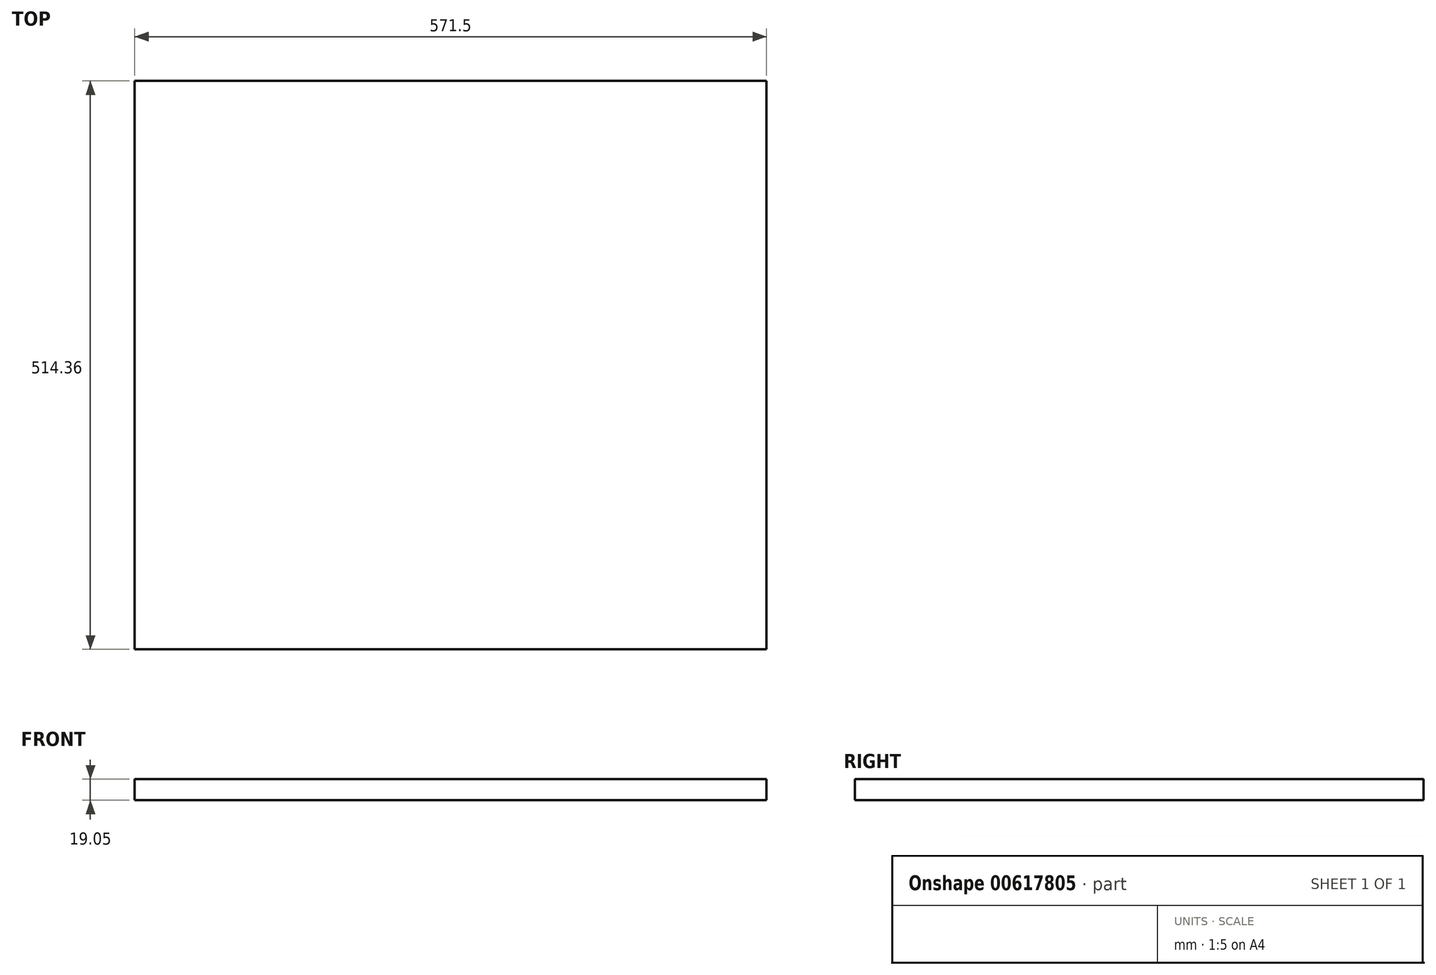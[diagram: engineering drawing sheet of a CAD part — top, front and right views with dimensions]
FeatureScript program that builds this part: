
annotation { "Feature Type Name" : "Feature", "Feature Type Description" : "" }
export const myFeature = defineFeature(function(context is Context, id is Id, definition is map)
    precondition{}
    {
        {
            var Q0;
            Q0=qCreatedBy(makeId("Top.planeOp"),FACE);
            var sketch = newSketch(context, id + "F0", { "sketchPlane" : qUnion([Q0])});
            skLineSegment(sketch, "E0.bottom", {"start": v(-285.75, 257.18) * mm, "end": v(285.75, 257.18) * mm});
            skLineSegment(sketch, "E0.top", {"start": v(-285.75, -257.18) * mm, "end": v(285.75, -257.18) * mm});
            skLineSegment(sketch, "E0.left", {"start": v(-285.75, 257.18) * mm, "end": v(-285.75, -257.18) * mm});
            skLineSegment(sketch, "E0.right", {"start": v(285.75, 257.18) * mm, "end": v(285.75, -257.18) * mm});
            skPoint(sketch, "E0.middle", {"position": v(0, 0) * mm});
            skSolve(sketch);
        }
        {
            var Q0;
            Q0=makeQuery(id+"F0.imprint","IMPRINT",FACE,{"disambiguationData":[TD([[makeQuery(id+"F0.imprint","IMPRINT",EDGE,{"derivedFrom":sQuery(id+"F0.wireOp",EDGE,"E0.bottom")}),-1.0]])]});
            extrude(context, id + "F1", {"entities" : qUnion([Q0]), "depth" : 19.05 * mm, "offsetDistance" : 25.4 * mm});
        }
    });
